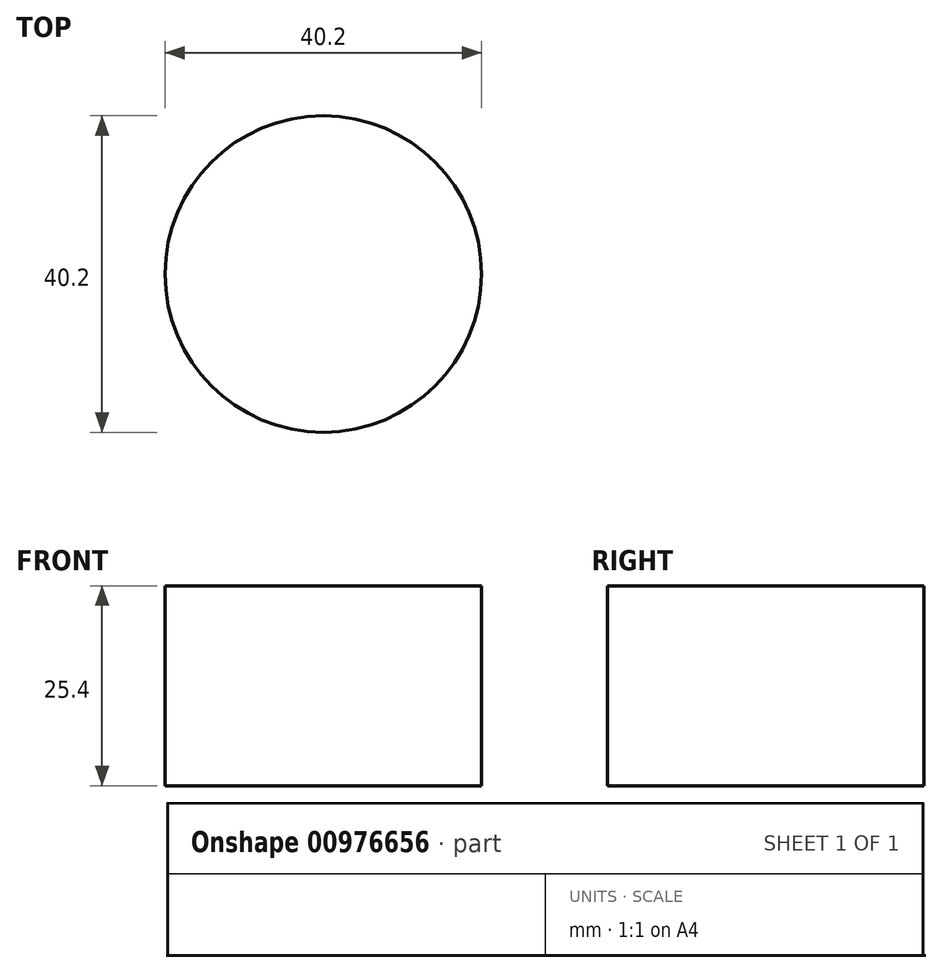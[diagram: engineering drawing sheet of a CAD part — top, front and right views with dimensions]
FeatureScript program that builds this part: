
annotation { "Feature Type Name" : "Feature", "Feature Type Description" : "" }
export const myFeature = defineFeature(function(context is Context, id is Id, definition is map)
    precondition{}
    {
        {
            var Q0;
            Q0=qCreatedBy(makeId("Top.planeOp"),FACE);
            var sketch = newSketch(context, id + "F0", { "sketchPlane" : qUnion([Q0])});
            skCircle(sketch, "E0", {"center": v(27.93, -52.45) * mm, "radius": 20.1 * mm});
            skSolve(sketch);
        }
        {
            var Q0;
            Q0=makeQuery(id+"F0.imprint","IMPRINT",FACE,{"disambiguationData":[TD([[makeQuery(id+"F0.imprint","IMPRINT",EDGE,{"derivedFrom":sQuery(id+"F0.wireOp",EDGE,"E0")}),1.0]])]});
            extrude(context, id + "F1", {"entities" : qUnion([Q0]), "depth" : 25.4 * mm, "offsetDistance" : 25.4 * mm});
        }
    });
